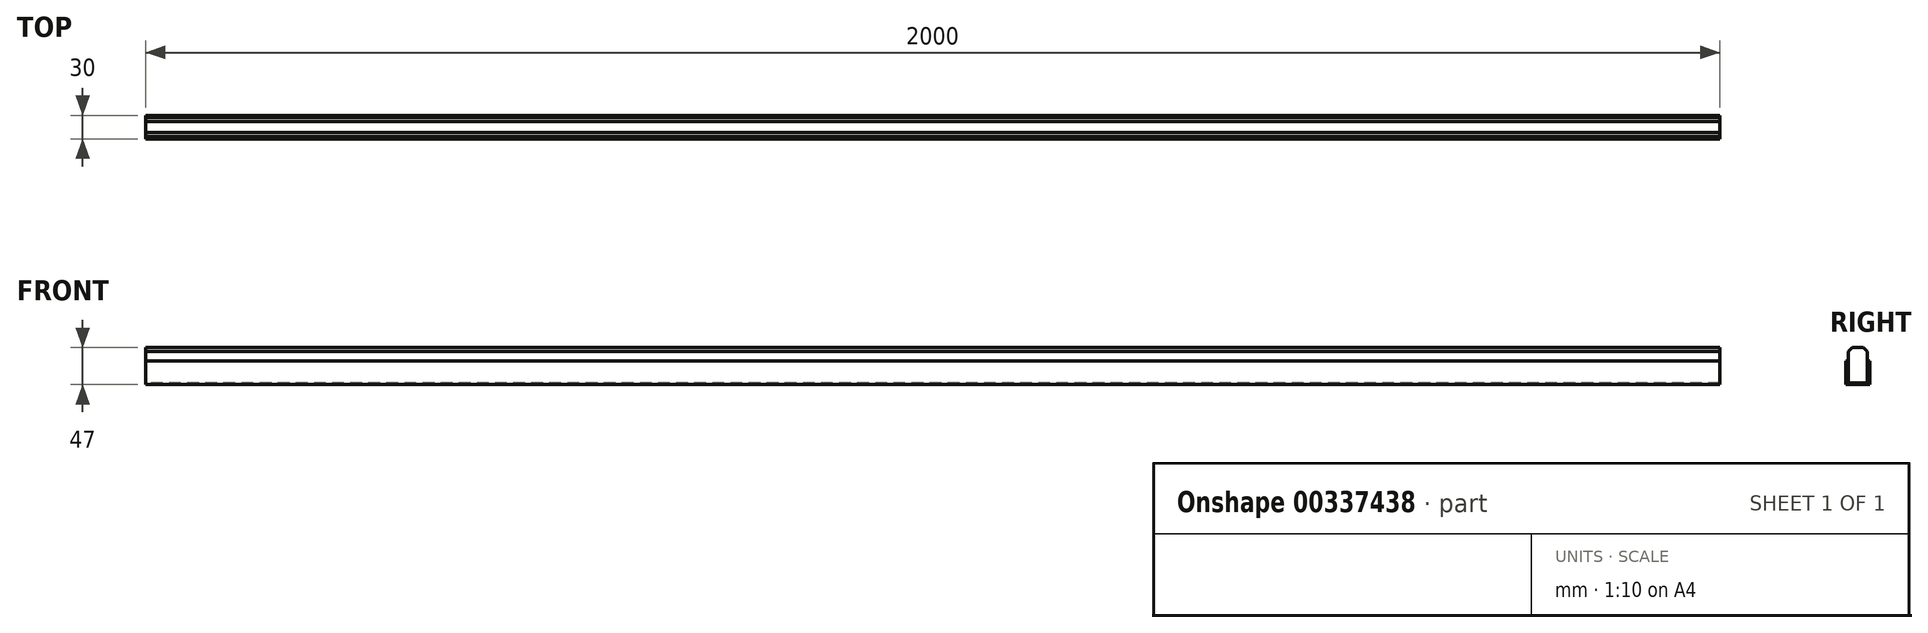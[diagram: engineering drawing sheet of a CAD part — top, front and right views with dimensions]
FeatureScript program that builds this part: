
annotation { "Feature Type Name" : "Feature", "Feature Type Description" : "" }
export const myFeature = defineFeature(function(context is Context, id is Id, definition is map)
    precondition{}
    {
        {
            var Q0;
            Q0=qCreatedBy(makeId("Right.planeOp"),FACE);
            var sketch = newSketch(context, id + "F0", { "sketchPlane" : qUnion([Q0])});
            skLineSegment(sketch, "E0", {"start": v(-20, 5.87) * mm, "end": v(-20, 35.87) * mm});
            skLineSegment(sketch, "E1", {"start": v(-20, 35.87) * mm, "end": v(-18, 35.87) * mm});
            skLineSegment(sketch, "E2", {"start": v(-18, 35.87) * mm, "end": v(-18, 7.87) * mm});
            skLineSegment(sketch, "E3.MirrorCS", {"start": v(10, 35.87) * mm, "end": v(8, 35.87) * mm});
            skLineSegment(sketch, "E4.MirrorCS", {"start": v(10, 5.87) * mm, "end": v(10, 35.87) * mm});
            skLineSegment(sketch, "E5.MirrorCS", {"start": v(8, 35.87) * mm, "end": v(8, 7.87) * mm});
            skLineSegment(sketch, "E6", {"start": v(-18, 7.87) * mm, "end": v(8, 7.87) * mm});
            skLineSegment(sketch, "E7", {"start": v(-20, 5.87) * mm, "end": v(10, 5.87) * mm});
            skLineSegment(sketch, "E8.0", {"start": v(7, 7.87) * mm, "end": v(7, 52.87) * mm});
            skLineSegment(sketch, "E9.0", {"start": v(-17, 7.87) * mm, "end": v(-17, 52.87) * mm});
            skLineSegment(sketch, "E10", {"start": v(7, 52.87) * mm, "end": v(-17, 52.87) * mm});
            skLineSegment(sketch, "E11", {"start": v(7, 7.87) * mm, "end": v(-17, 7.87) * mm});
            skSolve(sketch);
        }
        {
            var Q0;
            Q0=makeQuery(id+"F0.imprint","IMPRINT",FACE,{"disambiguationData":[TD([[makeQuery(id+"F0.imprint","IMPRINT",EDGE,{"derivedFrom":sQuery(id+"F0.wireOp",EDGE,"E8.0")}),1.0]])]});
            extrude(context, id + "F1", {"entities" : qUnion([Q0]), "endBound" : BoundingType.SYMMETRIC, "depth" : 2000 * mm});
        }
        {
            var Q0;
            Q0=makeQuery(id+"F0.imprint","IMPRINT",FACE,{"disambiguationData":[TD([[makeQuery(id+"F0.imprint","IMPRINT",EDGE,{"derivedFrom":sQuery(id+"F0.wireOp",EDGE,"E0")}),-1.0]])]});
            extrude(context, id + "F2", {"entities" : qUnion([Q0]), "endBound" : BoundingType.SYMMETRIC, "depth" : 2000 * mm});
        }
        {
            var Q0;
            Q0=makeQuery(id+"F1.opExtrude","SWEPT_EDGE",EDGE,{"disambiguationData":[OSD([sQuery(id+"F0.wireOp",EDGE,"E9.0"),sQuery(id+"F0.wireOp",EDGE,"E10")])]});
            var Q1;
            Q1=makeQuery(id+"F1.opExtrude","SWEPT_EDGE",EDGE,{"disambiguationData":[OSD([sQuery(id+"F0.wireOp",EDGE,"E8.0"),sQuery(id+"F0.wireOp",EDGE,"E10")])]});
            chamfer(context, id + "F3", {"entities" : qUnion([Q0, Q1]), "width" : 5 * mm, "tangentPropagation" : true});
        }
    });
